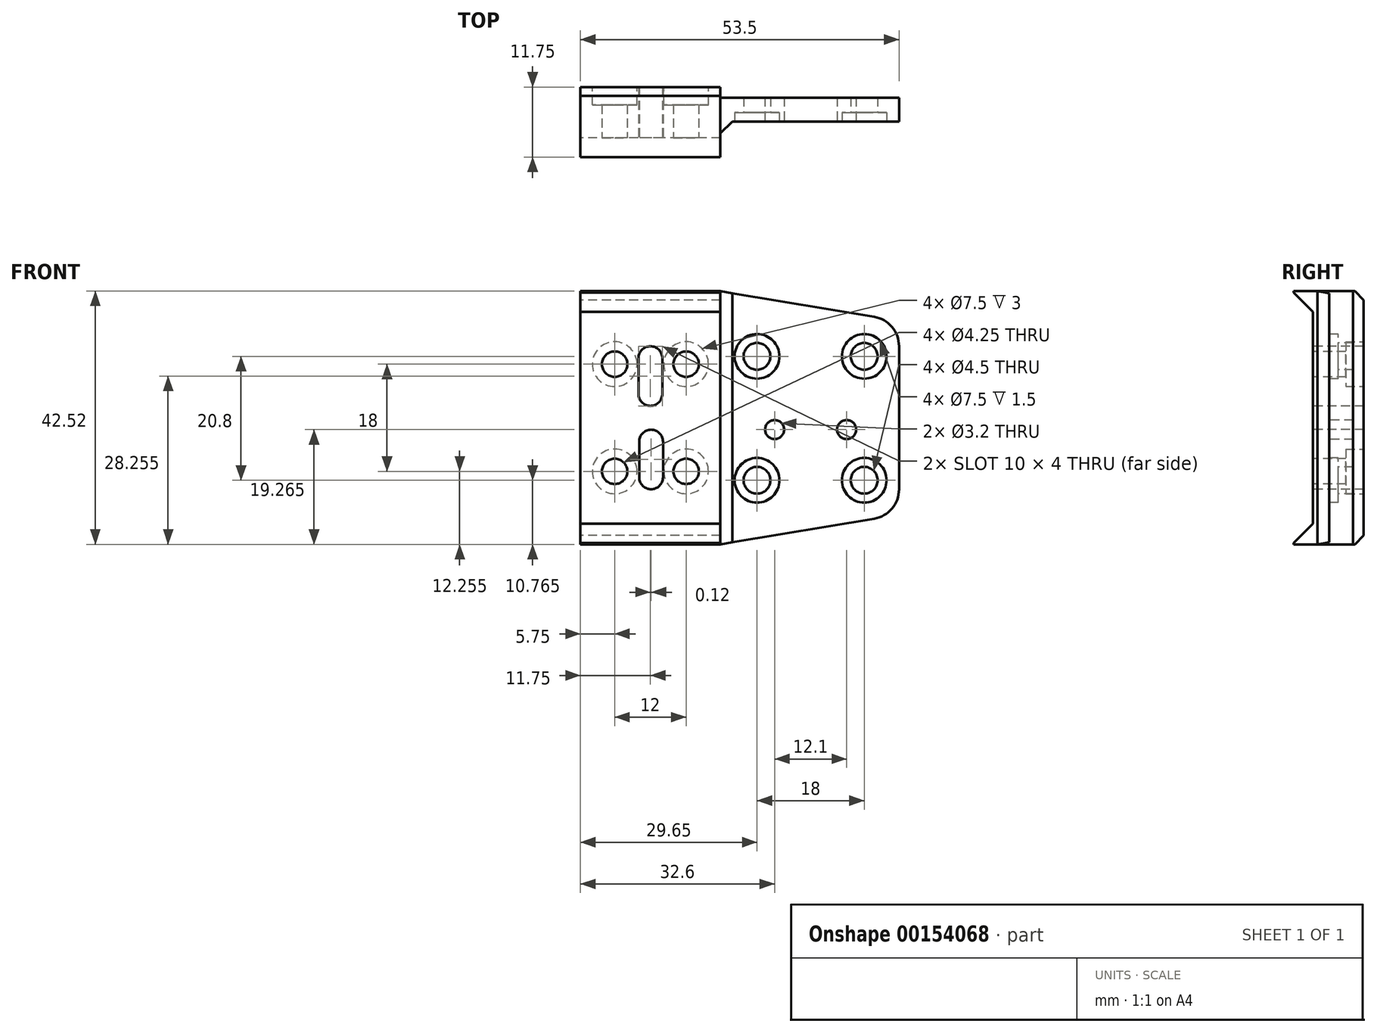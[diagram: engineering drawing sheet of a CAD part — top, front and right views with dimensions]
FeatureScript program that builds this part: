
annotation { "Feature Type Name" : "Feature", "Feature Type Description" : "" }
export const myFeature = defineFeature(function(context is Context, id is Id, definition is map)
    precondition{}
    {
        {
            var Q0;
            Q0=qCreatedBy(makeId("Front.planeOp"),FACE);
            var sketch = newSketch(context, id + "F0", { "sketchPlane" : qUnion([Q0])});
            skLineSegment(sketch, "E0.bottom", {"start": v(11.75, -21.26) * mm, "end": v(-11.75, -21.26) * mm});
            skLineSegment(sketch, "E0.top", {"start": v(11.75, 21.25) * mm, "end": v(-11.75, 21.25) * mm});
            skLineSegment(sketch, "E0.left", {"start": v(11.75, -21.25) * mm, "end": v(11.75, 21.26) * mm});
            skLineSegment(sketch, "E0.right", {"start": v(-11.75, -21.26) * mm, "end": v(-11.75, 21.25) * mm});
            skPoint(sketch, "E0.middle", {"position": v(0, 0) * mm});
            skSolve(sketch);
        }
        {
            var Q0;
            Q0 = qSketchRegion(id + "F0", true);
            extrude(context, id + "F1", {"entities" : qUnion([Q0]), "depth" : 9 * mm});
        }
        {
            var Q0;
            Q0=makeQuery(id+"F1.opExtrude","CAP_FACE",FACE,{"disambiguationData":[OSD([sQuery(id+"F0.wireOp",EDGE,"E0.bottom"),sQuery(id+"F0.wireOp",EDGE,"E0.top"),sQuery(id+"F0.wireOp",EDGE,"E0.left"),sQuery(id+"F0.wireOp",EDGE,"E0.right")])],"isStart":false});
            var sketch = newSketch(context, id + "F2", { "sketchPlane" : qUnion([Q0])});
            skCircle(sketch, "E1", {"center": v(-6, 9) * mm, "radius": 2.12 * mm});
            skCircle(sketch, "E2.1.0.0", {"center": v(6, 9) * mm, "radius": 2.12 * mm});
            skLineSegment(sketch, "E2.direction1", {"start": v(-6, 9) * mm, "end": v(6, 9) * mm, "construction": true});
            skCircle(sketch, "E3.1.0.0", {"center": v(-6, -9) * mm, "radius": 2.12 * mm});
            skCircle(sketch, "E3.1.0.1", {"center": v(6, -9) * mm, "radius": 2.12 * mm});
            skLineSegment(sketch, "E3.direction1", {"start": v(-6, -9) * mm, "end": v(-6, 9) * mm, "construction": true});
            skArc(sketch, "E4", {"start": v(2, 10) * mm, "mid": v(0, 12) * mm, "end": v(-2, 10) * mm});
            skLineSegment(sketch, "E5.left", {"start": v(2, 10) * mm, "end": v(2, 4) * mm});
            skLineSegment(sketch, "E5.right", {"start": v(-2, 10) * mm, "end": v(-2, 4) * mm});
            skArc(sketch, "E6", {"start": v(-2, 4) * mm, "mid": v(0, 2) * mm, "end": v(2, 4) * mm});
            skArc(sketch, "E7.1.0.0", {"start": v(2.12, -4) * mm, "mid": v(0.12, -2) * mm, "end": v(-1.88, -4) * mm});
            skLineSegment(sketch, "E7.1.0.1", {"start": v(2.12, -4) * mm, "end": v(2.12, -10) * mm});
            skArc(sketch, "E7.1.0.2", {"start": v(-1.88, -10) * mm, "mid": v(0.12, -12) * mm, "end": v(2.12, -10) * mm});
            skLineSegment(sketch, "E7.1.0.3", {"start": v(-1.88, -4) * mm, "end": v(-1.88, -10) * mm});
            skLineSegment(sketch, "E7.direction1", {"start": v(-2, 10) * mm, "end": v(-1.88, -4) * mm, "construction": true});
            skSolve(sketch);
        }
        {
            var Q0;
            Q0=makeQuery(id+"F2.imprint","IMPRINT",FACE,{"disambiguationData":[TD([[makeQuery(id+"F2.imprint","IMPRINT",EDGE,{"derivedFrom":sQuery(id+"F2.wireOp",EDGE,"E1")}),1.0]])]});
            var Q1;
            Q1=makeQuery(id+"F2.imprint","IMPRINT",FACE,{"disambiguationData":[TD([[makeQuery(id+"F2.imprint","IMPRINT",EDGE,{"derivedFrom":sQuery(id+"F2.wireOp",EDGE,"E4")}),1.0]])]});
            var Q2;
            Q2=makeQuery(id+"F2.imprint","IMPRINT",FACE,{"disambiguationData":[TD([[makeQuery(id+"F2.imprint","IMPRINT",EDGE,{"derivedFrom":sQuery(id+"F2.wireOp",EDGE,"E2.1.0.0")}),1.0]])]});
            var Q3;
            Q3=makeQuery(id+"F2.imprint","IMPRINT",FACE,{"disambiguationData":[TD([[makeQuery(id+"F2.imprint","IMPRINT",EDGE,{"derivedFrom":sQuery(id+"F2.wireOp",EDGE,"E3.1.0.1")}),1.0]])]});
            var Q4;
            Q4=makeQuery(id+"F2.imprint","IMPRINT",FACE,{"disambiguationData":[TD([[makeQuery(id+"F2.imprint","IMPRINT",EDGE,{"derivedFrom":sQuery(id+"F2.wireOp",EDGE,"E7.1.0.0")}),1.0]])]});
            var Q5;
            Q5=makeQuery(id+"F2.imprint","IMPRINT",FACE,{"disambiguationData":[TD([[makeQuery(id+"F2.imprint","IMPRINT",EDGE,{"derivedFrom":sQuery(id+"F2.wireOp",EDGE,"E3.1.0.0")}),1.0]])]});
            extrude(context, id + "F3", {"entities" : qUnion([Q0, Q1, Q2, Q3, Q4, Q5]), "operationType" : NewBodyOperationType.REMOVE, "endBound" : BoundingType.THROUGH_ALL, "oppositeDirection" : true, "depth" : 25 * mm});
        }
        {
            var Q0;
            Q0=makeQuery(id+"F1.opExtrude","SWEPT_FACE",FACE,{"disambiguationData":[OSD([sQuery(id+"F0.wireOp",EDGE,"E0.right")])]});
            var sketch = newSketch(context, id + "F4", { "sketchPlane" : qUnion([Q0])});
            skLineSegment(sketch, "E8", {"start": v(9, 21.25) * mm, "end": v(12.25, 21.25) * mm});
            skLineSegment(sketch, "E9", {"start": v(12.25, 21.25) * mm, "end": v(12.25, 21) * mm});
            skLineSegment(sketch, "E10", {"start": v(12.25, 21) * mm, "end": v(9, 17.75) * mm});
            skLineSegment(sketch, "E11", {"start": v(9, 17.75) * mm, "end": v(9, 21.25) * mm});
            skLineSegment(sketch, "E12", {"start": v(0, 0) * mm, "end": v(9, 0) * mm});
            skLineSegment(sketch, "E13.MirrorCS", {"start": v(9, -21.26) * mm, "end": v(12.25, -21.26) * mm});
            skLineSegment(sketch, "E14.MirrorCS", {"start": v(9, -17.76) * mm, "end": v(9, -21.26) * mm});
            skLineSegment(sketch, "E15.MirrorCS", {"start": v(12.25, -21) * mm, "end": v(9, -17.76) * mm});
            skLineSegment(sketch, "E16.MirrorCS", {"start": v(12.25, -21.26) * mm, "end": v(12.25, -21) * mm});
            skSolve(sketch);
        }
        {
            var Q0;
            Q0=makeQuery(id+"F4.imprint","IMPRINT",FACE,{"disambiguationData":[TD([[makeQuery(id+"F4.imprint","IMPRINT",EDGE,{"derivedFrom":sQuery(id+"F4.wireOp",EDGE,"E8")}),-1.0]])]});
            var Q1;
            Q1=makeQuery(id+"F4.imprint","IMPRINT",FACE,{"disambiguationData":[TD([[makeQuery(id+"F4.imprint","IMPRINT",EDGE,{"derivedFrom":sQuery(id+"F4.wireOp",EDGE,"E13.MirrorCS")}),1.0]])]});
            extrude(context, id + "F5", {"entities" : qUnion([Q0, Q1]), "operationType" : NewBodyOperationType.ADD, "oppositeDirection" : true, "depth" : 23.5 * mm});
        }
        {
            var Q0;
            Q0=makeQuery(id+"F1.opExtrude","CAP_EDGE",EDGE,{"disambiguationData":[OSD([sQuery(id+"F0.wireOp",EDGE,"E0.top")])],"isStart":true});
            var Q1;
            Q1=makeQuery(id+"F1.opExtrude","CAP_EDGE",EDGE,{"disambiguationData":[OSD([sQuery(id+"F0.wireOp",EDGE,"E0.bottom")])],"isStart":true});
            chamfer(context, id + "F6", {"entities" : qUnion([Q0, Q1]), "width" : 2 * mm, "tangentPropagation" : true});
        }
        {
            var Q0;
            Q0=makeQuery(id+"F5.boolean.opBoolean","MERGE",FACE,{"derivedFrom":[makeQuery(id+"F1.opExtrude","SWEPT_FACE",FACE,{"disambiguationData":[OSD([sQuery(id+"F0.wireOp",EDGE,"E0.left")])]}),makeQuery(id+"F5.opExtrude","CAP_FACE",FACE,{"disambiguationData":[OSD([sQuery(id+"F4.wireOp",EDGE,"E8"),sQuery(id+"F4.wireOp",EDGE,"E9"),sQuery(id+"F4.wireOp",EDGE,"E10"),sQuery(id+"F4.wireOp",EDGE,"E11")])],"isStart":false}),makeQuery(id+"F5.opExtrude","CAP_FACE",FACE,{"disambiguationData":[OSD([sQuery(id+"F4.wireOp",EDGE,"E13.MirrorCS"),sQuery(id+"F4.wireOp",EDGE,"E14.MirrorCS"),sQuery(id+"F4.wireOp",EDGE,"E15.MirrorCS"),sQuery(id+"F4.wireOp",EDGE,"E16.MirrorCS")])],"isStart":false})]});
            var sketch = newSketch(context, id + "F7", { "sketchPlane" : qUnion([Q0])});
            skLineSegment(sketch, "E17.bottom", {"start": v(-2.27, 21.25) * mm, "end": v(-6.27, 21.25) * mm});
            skLineSegment(sketch, "E17.top", {"start": v(-2.27, -21.25) * mm, "end": v(-6.27, -21.25) * mm});
            skLineSegment(sketch, "E17.left", {"start": v(-2.27, 21.25) * mm, "end": v(-2.27, -21.25) * mm});
            skLineSegment(sketch, "E17.right", {"start": v(-6.27, 21.25) * mm, "end": v(-6.27, -21.25) * mm});
            skSolve(sketch);
        }
        {
            var Q0;
            Q0=makeQuery(id+"F7.imprint","IMPRINT",FACE,{"disambiguationData":[TD([[makeQuery(id+"F7.imprint","IMPRINT",EDGE,{"derivedFrom":sQuery(id+"F7.wireOp",EDGE,"E17.bottom")}),1.0]])]});
            extrude(context, id + "F8", {"entities" : qUnion([Q0]), "operationType" : NewBodyOperationType.ADD, "depth" : 30 * mm});
        }
        {
            var Q0;
            Q0=makeQuery(id+"F8.opExtrude","SWEPT_FACE",FACE,{"disambiguationData":[OSD([sQuery(id+"F7.wireOp",EDGE,"E17.right")])]});
            var sketch = newSketch(context, id + "F9", { "sketchPlane" : qUnion([Q0])});
            skCircle(sketch, "E18", {"center": v(17.9, -10.5) * mm, "radius": 2.25 * mm});
            skCircle(sketch, "E19.0.1.0", {"center": v(17.9, 10.3) * mm, "radius": 2.25 * mm});
            skCircle(sketch, "E19.1.0.0", {"center": v(35.9, -10.5) * mm, "radius": 2.25 * mm});
            skCircle(sketch, "E19.1.1.0", {"center": v(35.9, 10.3) * mm, "radius": 2.25 * mm});
            skLineSegment(sketch, "E19.direction1", {"start": v(17.9, -10.5) * mm, "end": v(35.9, -10.5) * mm, "construction": true});
            skLineSegment(sketch, "E19.direction2", {"start": v(17.9, -10.5) * mm, "end": v(17.9, 10.3) * mm, "construction": true});
            skCircle(sketch, "E20", {"center": v(32.95, -2) * mm, "radius": 1.6 * mm});
            skCircle(sketch, "E21.1.0.0", {"center": v(20.85, -2) * mm, "radius": 1.6 * mm});
            skLineSegment(sketch, "E21.direction1", {"start": v(32.95, -2) * mm, "end": v(20.85, -2) * mm, "construction": true});
            skSolve(sketch);
        }
        {
            var Q0;
            Q0=makeQuery(id+"F9.imprint","IMPRINT",FACE,{"disambiguationData":[TD([[makeQuery(id+"F9.imprint","IMPRINT",EDGE,{"derivedFrom":sQuery(id+"F9.wireOp",EDGE,"E19.0.1.0")}),1.0]])]});
            var Q1;
            Q1=makeQuery(id+"F9.imprint","IMPRINT",FACE,{"disambiguationData":[TD([[makeQuery(id+"F9.imprint","IMPRINT",EDGE,{"derivedFrom":sQuery(id+"F9.wireOp",EDGE,"E19.1.1.0")}),1.0]])]});
            var Q2;
            Q2=makeQuery(id+"F9.imprint","IMPRINT",FACE,{"disambiguationData":[TD([[makeQuery(id+"F9.imprint","IMPRINT",EDGE,{"derivedFrom":sQuery(id+"F9.wireOp",EDGE,"E21.1.0.0")}),1.0]])]});
            var Q3;
            Q3=makeQuery(id+"F9.imprint","IMPRINT",FACE,{"disambiguationData":[TD([[makeQuery(id+"F9.imprint","IMPRINT",EDGE,{"derivedFrom":sQuery(id+"F9.wireOp",EDGE,"E20")}),1.0]])]});
            var Q4;
            Q4=makeQuery(id+"F9.imprint","IMPRINT",FACE,{"disambiguationData":[TD([[makeQuery(id+"F9.imprint","IMPRINT",EDGE,{"derivedFrom":sQuery(id+"F9.wireOp",EDGE,"E18")}),1.0]])]});
            var Q5;
            Q5=makeQuery(id+"F9.imprint","IMPRINT",FACE,{"disambiguationData":[TD([[makeQuery(id+"F9.imprint","IMPRINT",EDGE,{"derivedFrom":sQuery(id+"F9.wireOp",EDGE,"E19.1.0.0")}),1.0]])]});
            extrude(context, id + "F10", {"entities" : qUnion([Q0, Q1, Q2, Q3, Q4, Q5]), "operationType" : NewBodyOperationType.REMOVE, "endBound" : BoundingType.THROUGH_ALL, "oppositeDirection" : true, "depth" : 25 * mm});
        }
        {
            var Q0;
            Q0=makeQuery(id+"F8.opExtrude","SWEPT_FACE",FACE,{"disambiguationData":[OSD([sQuery(id+"F7.wireOp",EDGE,"E17.right")])]});
            var sketch = newSketch(context, id + "F11", { "sketchPlane" : qUnion([Q0])});
            skCircle(sketch, "E22", {"center": v(17.9, 10.3) * mm, "radius": 3.75 * mm});
            skCircle(sketch, "E23", {"center": v(35.9, 10.3) * mm, "radius": 3.75 * mm});
            skCircle(sketch, "E24", {"center": v(35.9, -10.5) * mm, "radius": 3.75 * mm});
            skCircle(sketch, "E25", {"center": v(17.9, -10.5) * mm, "radius": 3.75 * mm});
            skSolve(sketch);
        }
        {
            var Q0;
            Q0=makeQuery(id+"F11.imprint","IMPRINT",FACE,{"disambiguationData":[TD([[makeQuery(id+"F11.imprint","IMPRINT",EDGE,{"derivedFrom":sQuery(id+"F11.wireOp",EDGE,"E22")}),1.0]])]});
            var Q1;
            Q1=makeQuery(id+"F11.imprint","IMPRINT",FACE,{"disambiguationData":[TD([[makeQuery(id+"F11.imprint","IMPRINT",EDGE,{"derivedFrom":sQuery(id+"F11.wireOp",EDGE,"E23")}),1.0]])]});
            var Q2;
            Q2=makeQuery(id+"F11.imprint","IMPRINT",FACE,{"disambiguationData":[TD([[makeQuery(id+"F11.imprint","IMPRINT",EDGE,{"derivedFrom":sQuery(id+"F11.wireOp",EDGE,"E24")}),1.0]])]});
            var Q3;
            Q3=makeQuery(id+"F11.imprint","IMPRINT",FACE,{"disambiguationData":[TD([[makeQuery(id+"F11.imprint","IMPRINT",EDGE,{"derivedFrom":sQuery(id+"F11.wireOp",EDGE,"E25")}),1.0]])]});
            extrude(context, id + "F12", {"entities" : qUnion([Q0, Q1, Q2, Q3]), "operationType" : NewBodyOperationType.REMOVE, "oppositeDirection" : true, "depth" : 1.5 * mm});
        }
        {
            var Q0;
            Q0=makeQuery(id+"F8.opExtrude","CAP_EDGE",EDGE,{"disambiguationData":[OSD([sQuery(id+"F7.wireOp",EDGE,"E17.bottom")])],"isStart":false});
            var Q1;
            Q1=makeQuery(id+"F8.opExtrude","CAP_EDGE",EDGE,{"disambiguationData":[OSD([sQuery(id+"F7.wireOp",EDGE,"E17.top")])],"isStart":false});
            chamfer(context, id + "F13", {"entities" : qUnion([Q0, Q1]), "chamferType" : ChamferType.TWO_OFFSETS, "width1" : 5 * mm, "oppositeDirection" : false, "width2" : 30 * mm, "tangentPropagation" : true});
        }
        {
            var Q0;
            {var subQ0=sQuery(id+"F7.wireOp",EDGE,"E17.bottom");Q0=makeQuery(id+"F13.opChamfer","BLEND_EDGE",EDGE,{"blendedFrom":[makeQuery(id+"F8.opExtrude","CAP_EDGE",EDGE,{"disambiguationData":[OSD([subQ0])],"isStart":false}),makeQuery(id+"F8.opExtrude","CAP_FACE",FACE,{"disambiguationData":[OSD([subQ0,sQuery(id+"F7.wireOp",EDGE,"E17.top"),sQuery(id+"F7.wireOp",EDGE,"E17.left"),sQuery(id+"F7.wireOp",EDGE,"E17.right")])],"isStart":false})],"blendedInto":[makeQuery(id+"F8.opExtrude","CAP_FACE",FACE,{"disambiguationData":[OSD([subQ0,sQuery(id+"F7.wireOp",EDGE,"E17.top"),sQuery(id+"F7.wireOp",EDGE,"E17.left"),sQuery(id+"F7.wireOp",EDGE,"E17.right")])],"isStart":false})]});}
            var Q1;
            {var subQ0=sQuery(id+"F7.wireOp",EDGE,"E17.top");Q1=makeQuery(id+"F13.opChamfer","BLEND_EDGE",EDGE,{"blendedFrom":[makeQuery(id+"F8.opExtrude","CAP_EDGE",EDGE,{"disambiguationData":[OSD([subQ0])],"isStart":false}),makeQuery(id+"F8.opExtrude","CAP_FACE",FACE,{"disambiguationData":[OSD([sQuery(id+"F7.wireOp",EDGE,"E17.bottom"),subQ0,sQuery(id+"F7.wireOp",EDGE,"E17.left"),sQuery(id+"F7.wireOp",EDGE,"E17.right")])],"isStart":false})],"blendedInto":[makeQuery(id+"F8.opExtrude","CAP_FACE",FACE,{"disambiguationData":[OSD([sQuery(id+"F7.wireOp",EDGE,"E17.bottom"),subQ0,sQuery(id+"F7.wireOp",EDGE,"E17.left"),sQuery(id+"F7.wireOp",EDGE,"E17.right")])],"isStart":false})]});}
            fillet(context, id + "F14", {"entities" : qUnion([Q0, Q1]), "radius" : 5 * mm, "tangentPropagation" : true, "allowEdgeOverflow" : false});
        }
        {
            var Q0;
            Q0=makeQuery(id+"F8.opExtrude","CAP_EDGE",EDGE,{"disambiguationData":[OSD([sQuery(id+"F7.wireOp",EDGE,"E17.right")])],"isStart":true});
            chamfer(context, id + "F15", {"entities" : qUnion([Q0]), "width" : 2 * mm, "tangentPropagation" : true});
        }
        {
            var Q0;
            Q0=makeQuery(id+"F1.opExtrude","CAP_FACE",FACE,{"disambiguationData":[OSD([sQuery(id+"F0.wireOp",EDGE,"E0.bottom"),sQuery(id+"F0.wireOp",EDGE,"E0.top"),sQuery(id+"F0.wireOp",EDGE,"E0.left"),sQuery(id+"F0.wireOp",EDGE,"E0.right")])],"isStart":true});
            var sketch = newSketch(context, id + "F16", { "sketchPlane" : qUnion([Q0])});
            skCircle(sketch, "E26", {"center": v(-6, 9) * mm, "radius": 3.75 * mm});
            skCircle(sketch, "E27", {"center": v(6, 9) * mm, "radius": 3.75 * mm});
            skCircle(sketch, "E28", {"center": v(6, -9) * mm, "radius": 3.75 * mm});
            skCircle(sketch, "E29", {"center": v(-6, -9) * mm, "radius": 3.75 * mm});
            skSolve(sketch);
        }
        {
            var Q0;
            Q0=makeQuery(id+"F16.imprint","IMPRINT",FACE,{"disambiguationData":[TD([[makeQuery(id+"F16.imprint","IMPRINT",EDGE,{"derivedFrom":sQuery(id+"F16.wireOp",EDGE,"E26")}),1.0]])]});
            var Q1;
            Q1=makeQuery(id+"F16.imprint","IMPRINT",FACE,{"disambiguationData":[TD([[makeQuery(id+"F16.imprint","IMPRINT",EDGE,{"derivedFrom":sQuery(id+"F16.wireOp",EDGE,"E27")}),1.0]])]});
            var Q2;
            Q2=makeQuery(id+"F16.imprint","IMPRINT",FACE,{"disambiguationData":[TD([[makeQuery(id+"F16.imprint","IMPRINT",EDGE,{"derivedFrom":sQuery(id+"F16.wireOp",EDGE,"E29")}),1.0]])]});
            var Q3;
            Q3=makeQuery(id+"F16.imprint","IMPRINT",FACE,{"disambiguationData":[TD([[makeQuery(id+"F16.imprint","IMPRINT",EDGE,{"derivedFrom":sQuery(id+"F16.wireOp",EDGE,"E28")}),1.0]])]});
            extrude(context, id + "F17", {"entities" : qUnion([Q0, Q1, Q2, Q3]), "operationType" : NewBodyOperationType.REMOVE, "oppositeDirection" : true, "depth" : 3.5 * mm});
        }
        {
            var Q0;
            Q0=makeQuery(id+"F5.boolean.opBoolean","MERGE",FACE,{"derivedFrom":[makeQuery(id+"F1.opExtrude","SWEPT_FACE",FACE,{"disambiguationData":[OSD([sQuery(id+"F0.wireOp",EDGE,"E0.right")])]}),makeQuery(id+"F5.opExtrude","CAP_FACE",FACE,{"disambiguationData":[OSD([sQuery(id+"F4.wireOp",EDGE,"E8"),sQuery(id+"F4.wireOp",EDGE,"E9"),sQuery(id+"F4.wireOp",EDGE,"E10"),sQuery(id+"F4.wireOp",EDGE,"E11")])],"isStart":true}),makeQuery(id+"F5.opExtrude","CAP_FACE",FACE,{"disambiguationData":[OSD([sQuery(id+"F4.wireOp",EDGE,"E13.MirrorCS"),sQuery(id+"F4.wireOp",EDGE,"E14.MirrorCS"),sQuery(id+"F4.wireOp",EDGE,"E15.MirrorCS"),sQuery(id+"F4.wireOp",EDGE,"E16.MirrorCS")])],"isStart":true})]});
            var sketch = newSketch(context, id + "F18", { "sketchPlane" : qUnion([Q0])});
            skLineSegment(sketch, "E30", {"start": v(0.5, 19.75) * mm, "end": v(0.5, -19.76) * mm});
            skLineSegment(sketch, "E31", {"start": v(0.5, -19.76) * mm, "end": v(0, -19.26) * mm});
            skLineSegment(sketch, "E32", {"start": v(0, -19.26) * mm, "end": v(0, 19.26) * mm});
            skLineSegment(sketch, "E33", {"start": v(0, 19.26) * mm, "end": v(0.5, 19.75) * mm});
            skSolve(sketch);
        }
        {
            var Q0;
            Q0 = qSketchRegion(id + "F18", true);
            extrude(context, id + "F19", {"entities" : qUnion([Q0]), "operationType" : NewBodyOperationType.REMOVE, "endBound" : BoundingType.THROUGH_ALL, "oppositeDirection" : true, "depth" : 25 * mm});
        }
    });
